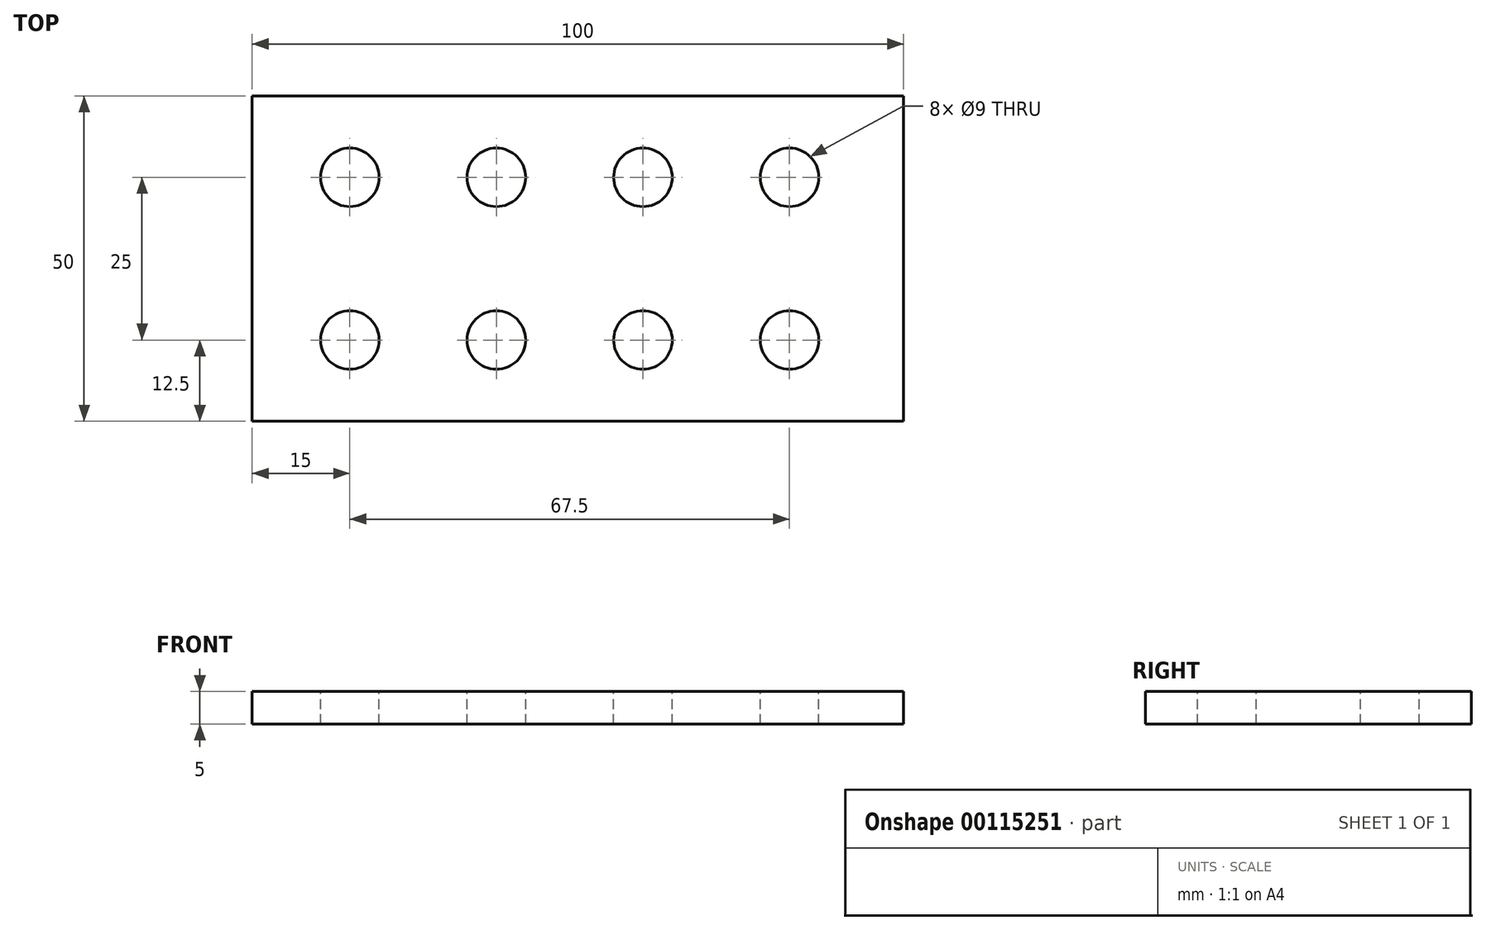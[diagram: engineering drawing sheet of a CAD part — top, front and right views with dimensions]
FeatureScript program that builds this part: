
annotation { "Feature Type Name" : "Feature", "Feature Type Description" : "" }
export const myFeature = defineFeature(function(context is Context, id is Id, definition is map)
    precondition{}
    {
        {
            var Q0;
            Q0=qCreatedBy(makeId("Top.planeOp"),FACE);
            var sketch = newSketch(context, id + "F0", { "sketchPlane" : qUnion([Q0])});
            skLineSegment(sketch, "E0.bottom", {"start": v(50, -25) * mm, "end": v(-50, -25) * mm});
            skLineSegment(sketch, "E0.top", {"start": v(50, 25) * mm, "end": v(-50, 25) * mm});
            skLineSegment(sketch, "E0.left", {"start": v(50, -25) * mm, "end": v(50, 25) * mm});
            skLineSegment(sketch, "E0.right", {"start": v(-50, -25) * mm, "end": v(-50, 25) * mm});
            skPoint(sketch, "E0.middle", {"position": v(0, 0) * mm});
            skSolve(sketch);
        }
        {
            var Q0;
            Q0 = qSketchRegion(id + "F0", true);
            extrude(context, id + "F1", {"entities" : qUnion([Q0]), "depth" : 5 * mm});
        }
        {
            var Q0;
            Q0=makeQuery(id+"F1.opExtrude","CAP_FACE",FACE,{"disambiguationData":[OSD([sQuery(id+"F0.wireOp",EDGE,"E0.bottom"),sQuery(id+"F0.wireOp",EDGE,"E0.top"),sQuery(id+"F0.wireOp",EDGE,"E0.left"),sQuery(id+"F0.wireOp",EDGE,"E0.right")])],"isStart":false});
            var sketch = newSketch(context, id + "F2", { "sketchPlane" : qUnion([Q0])});
            skCircle(sketch, "E1", {"center": v(32.5, 12.5) * mm, "radius": 4.5 * mm});
            skCircle(sketch, "E2.0.1.0", {"center": v(32.5, -12.5) * mm, "radius": 4.5 * mm});
            skCircle(sketch, "E2.1.0.0", {"center": v(10, 12.5) * mm, "radius": 4.5 * mm});
            skCircle(sketch, "E2.1.1.0", {"center": v(10, -12.5) * mm, "radius": 4.5 * mm});
            skCircle(sketch, "E2.2.0.0", {"center": v(-12.5, 12.5) * mm, "radius": 4.5 * mm});
            skCircle(sketch, "E2.2.1.0", {"center": v(-12.5, -12.5) * mm, "radius": 4.5 * mm});
            skLineSegment(sketch, "E2.direction1", {"start": v(37.5, 12.5) * mm, "end": v(17.5, 12.5) * mm, "construction": true});
            skLineSegment(sketch, "E2.direction2", {"start": v(37.5, 12.5) * mm, "end": v(37.5, -12.5) * mm, "construction": true});
            skCircle(sketch, "E3.0.3.0", {"center": v(-35, 12.5) * mm, "radius": 4.5 * mm});
            skCircle(sketch, "E3.0.3.1", {"center": v(-35, -12.5) * mm, "radius": 4.5 * mm});
            skSolve(sketch);
        }
        {
            var Q0;
            Q0 = qSketchRegion(id + "F2", true);
            extrude(context, id + "F3", {"entities" : qUnion([Q0]), "operationType" : NewBodyOperationType.REMOVE, "oppositeDirection" : true, "depth" : 25 * mm});
        }
    });
